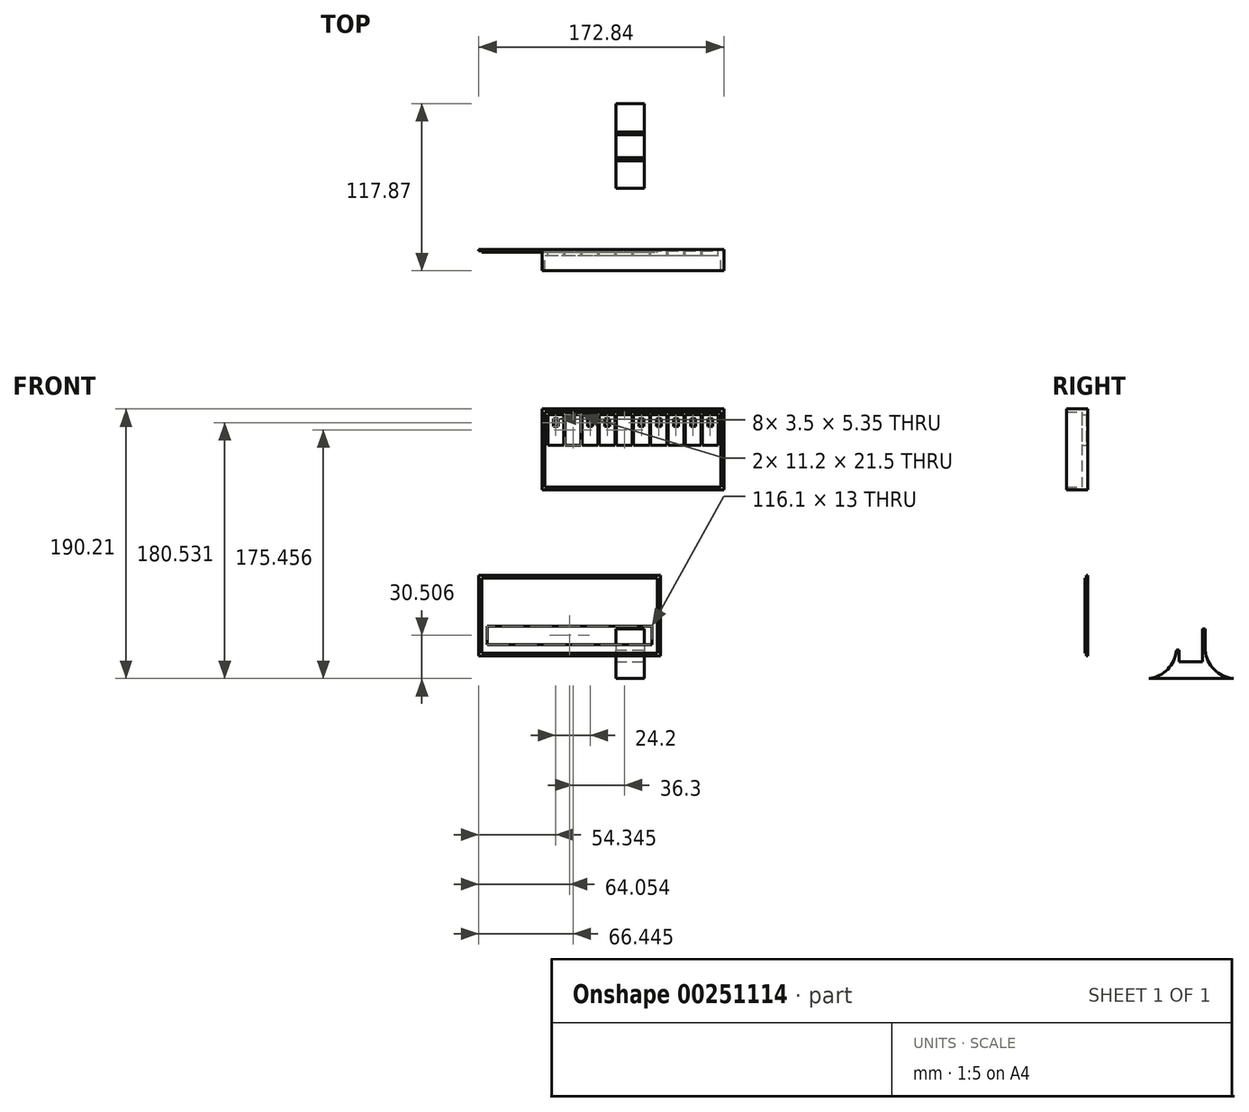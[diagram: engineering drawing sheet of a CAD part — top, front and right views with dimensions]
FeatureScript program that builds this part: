
annotation { "Feature Type Name" : "Feature", "Feature Type Description" : "" }
export const myFeature = defineFeature(function(context is Context, id is Id, definition is map)
    precondition{}
    {
        {
            var Q0;
            Q0=qCreatedBy(makeId("Front.planeOp"),FACE);
            var sketch = newSketch(context, id + "F0", { "sketchPlane" : qUnion([Q0])});
            skLineSegment(sketch, "E0.bottom", {"start": v(-72.05, 26.77) * mm, "end": v(56.05, 26.77) * mm});
            skLineSegment(sketch, "E0.top", {"start": v(-72.05, -30.23) * mm, "end": v(56.05, -30.23) * mm});
            skLineSegment(sketch, "E0.left", {"start": v(-72.05, 26.77) * mm, "end": v(-72.05, -30.23) * mm});
            skLineSegment(sketch, "E0.right", {"start": v(56.05, 26.77) * mm, "end": v(56.05, -30.23) * mm});
            skLineSegment(sketch, "E1", {"start": v(-72.05, 26.77) * mm, "end": v(-70.05, 26.77) * mm});
            skLineSegment(sketch, "E2.bottom", {"start": v(-70.05, 24.77) * mm, "end": v(54.05, 24.77) * mm});
            skLineSegment(sketch, "E2.top", {"start": v(-70.05, -28.23) * mm, "end": v(54.05, -28.23) * mm});
            skLineSegment(sketch, "E2.left", {"start": v(-70.05, 24.77) * mm, "end": v(-70.05, -28.23) * mm});
            skLineSegment(sketch, "E2.right", {"start": v(54.05, 24.77) * mm, "end": v(54.05, -28.23) * mm});
            skLineSegment(sketch, "E3", {"start": v(-70.05, 24.77) * mm, "end": v(-68.05, 24.77) * mm});
            skLineSegment(sketch, "E4", {"start": v(-68.05, 22.77) * mm, "end": v(-56.85, 22.77) * mm});
            skLineSegment(sketch, "E5", {"start": v(-55.95, 22.77) * mm, "end": v(-44.75, 22.77) * mm});
            skLineSegment(sketch, "E6", {"start": v(-43.85, 22.77) * mm, "end": v(-32.65, 22.77) * mm});
            skLineSegment(sketch, "E7", {"start": v(-31.75, 22.77) * mm, "end": v(-20.55, 22.77) * mm});
            skLineSegment(sketch, "E8", {"start": v(-19.65, 22.77) * mm, "end": v(-8.45, 22.77) * mm});
            skLineSegment(sketch, "E9", {"start": v(-7.55, 22.77) * mm, "end": v(3.65, 22.77) * mm});
            skLineSegment(sketch, "E10", {"start": v(4.55, 22.77) * mm, "end": v(15.75, 22.77) * mm});
            skLineSegment(sketch, "E11", {"start": v(16.65, 22.77) * mm, "end": v(27.85, 22.77) * mm});
            skLineSegment(sketch, "E12", {"start": v(28.75, 22.77) * mm, "end": v(39.95, 22.77) * mm});
            skLineSegment(sketch, "E13", {"start": v(40.85, 22.77) * mm, "end": v(48.79, 22.77) * mm});
            skLineSegment(sketch, "E14.top", {"start": v(-68.05, 1.27) * mm, "end": v(-56.85, 1.27) * mm});
            skLineSegment(sketch, "E14.left", {"start": v(-68.05, 22.77) * mm, "end": v(-68.05, 1.27) * mm});
            skLineSegment(sketch, "E14.right", {"start": v(-56.85, 22.77) * mm, "end": v(-56.85, 1.27) * mm});
            skLineSegment(sketch, "E15.top", {"start": v(-55.95, 1.27) * mm, "end": v(-44.75, 1.27) * mm});
            skLineSegment(sketch, "E15.left", {"start": v(-55.95, 22.77) * mm, "end": v(-55.95, 1.27) * mm});
            skLineSegment(sketch, "E15.right", {"start": v(-44.75, 22.77) * mm, "end": v(-44.75, 1.27) * mm});
            skLineSegment(sketch, "E16.top", {"start": v(-43.85, 1.27) * mm, "end": v(-32.65, 1.27) * mm});
            skLineSegment(sketch, "E16.left", {"start": v(-43.85, 22.77) * mm, "end": v(-43.85, 1.27) * mm});
            skLineSegment(sketch, "E16.right", {"start": v(-32.65, 22.77) * mm, "end": v(-32.65, 1.27) * mm});
            skLineSegment(sketch, "E17.top", {"start": v(-31.75, 1.27) * mm, "end": v(-20.55, 1.27) * mm});
            skLineSegment(sketch, "E17.left", {"start": v(-31.75, 22.77) * mm, "end": v(-31.75, 1.27) * mm});
            skLineSegment(sketch, "E17.right", {"start": v(-20.55, 22.77) * mm, "end": v(-20.55, 1.27) * mm});
            skLineSegment(sketch, "E18.top", {"start": v(-19.65, 1.27) * mm, "end": v(-8.45, 1.27) * mm});
            skLineSegment(sketch, "E18.left", {"start": v(-19.65, 22.77) * mm, "end": v(-19.65, 1.27) * mm});
            skLineSegment(sketch, "E18.right", {"start": v(-8.45, 22.77) * mm, "end": v(-8.45, 1.27) * mm});
            skLineSegment(sketch, "E19.top", {"start": v(-7.55, 1.27) * mm, "end": v(3.65, 1.27) * mm});
            skLineSegment(sketch, "E19.left", {"start": v(-7.55, 22.77) * mm, "end": v(-7.55, 1.27) * mm});
            skLineSegment(sketch, "E19.right", {"start": v(3.65, 22.77) * mm, "end": v(3.65, 1.27) * mm});
            skLineSegment(sketch, "E20.top", {"start": v(4.55, 1.27) * mm, "end": v(15.75, 1.27) * mm});
            skLineSegment(sketch, "E20.left", {"start": v(4.55, 22.77) * mm, "end": v(4.55, 1.27) * mm});
            skLineSegment(sketch, "E20.right", {"start": v(15.75, 22.77) * mm, "end": v(15.75, 1.27) * mm});
            skLineSegment(sketch, "E21.top", {"start": v(16.65, 1.27) * mm, "end": v(27.85, 1.27) * mm});
            skLineSegment(sketch, "E21.left", {"start": v(16.65, 22.77) * mm, "end": v(16.65, 1.27) * mm});
            skLineSegment(sketch, "E21.right", {"start": v(27.85, 22.77) * mm, "end": v(27.85, 1.27) * mm});
            skLineSegment(sketch, "E22.top", {"start": v(28.75, 1.27) * mm, "end": v(39.95, 1.27) * mm});
            skLineSegment(sketch, "E22.left", {"start": v(28.75, 22.77) * mm, "end": v(28.75, 1.27) * mm});
            skLineSegment(sketch, "E22.right", {"start": v(39.95, 22.77) * mm, "end": v(39.95, 1.27) * mm});
            skLineSegment(sketch, "E23.bottom", {"start": v(40.85, 22.77) * mm, "end": v(52.05, 22.77) * mm});
            skLineSegment(sketch, "E23.top", {"start": v(40.85, 1.27) * mm, "end": v(52.05, 1.27) * mm});
            skLineSegment(sketch, "E23.left", {"start": v(40.85, 22.77) * mm, "end": v(40.85, 1.27) * mm});
            skLineSegment(sketch, "E23.right", {"start": v(52.05, 22.77) * mm, "end": v(52.05, 1.27) * mm});
            skLineSegment(sketch, "E24", {"start": v(-68.05, 22.77) * mm, "end": v(-64.2, 22.77) * mm});
            skLineSegment(sketch, "E25", {"start": v(-55.95, 22.77) * mm, "end": v(-52.1, 22.77) * mm});
            skLineSegment(sketch, "E26", {"start": v(-43.85, 22.77) * mm, "end": v(-40, 22.77) * mm});
            skLineSegment(sketch, "E27", {"start": v(-31.75, 22.77) * mm, "end": v(-27.9, 22.77) * mm});
            skLineSegment(sketch, "E28", {"start": v(-19.65, 22.77) * mm, "end": v(-15.8, 22.77) * mm});
            skLineSegment(sketch, "E29", {"start": v(-7.55, 22.77) * mm, "end": v(-3.7, 22.77) * mm});
            skLineSegment(sketch, "E30", {"start": v(4.55, 22.77) * mm, "end": v(8.4, 22.77) * mm});
            skLineSegment(sketch, "E31", {"start": v(16.65, 22.77) * mm, "end": v(20.5, 22.77) * mm});
            skLineSegment(sketch, "E32", {"start": v(28.75, 22.77) * mm, "end": v(32.6, 22.77) * mm});
            skLineSegment(sketch, "E33", {"start": v(40.85, 22.77) * mm, "end": v(44.7, 22.77) * mm});
            skLineSegment(sketch, "E34.bottom", {"start": v(-64.2, 19.77) * mm, "end": v(-60.7, 19.77) * mm});
            skLineSegment(sketch, "E34.top", {"start": v(-64.2, 14.42) * mm, "end": v(-60.7, 14.42) * mm});
            skLineSegment(sketch, "E34.left", {"start": v(-64.2, 19.77) * mm, "end": v(-64.2, 14.42) * mm});
            skLineSegment(sketch, "E34.right", {"start": v(-60.7, 19.77) * mm, "end": v(-60.7, 14.42) * mm});
            skLineSegment(sketch, "E35", {"start": v(-52.1, 22.77) * mm, "end": v(-52.1, 19.77) * mm});
            skLineSegment(sketch, "E36.bottom", {"start": v(-52.1, 19.77) * mm, "end": v(-48.6, 19.77) * mm});
            skLineSegment(sketch, "E36.top", {"start": v(-52.1, 14.42) * mm, "end": v(-48.6, 14.42) * mm});
            skLineSegment(sketch, "E36.left", {"start": v(-52.1, 19.77) * mm, "end": v(-52.1, 14.42) * mm});
            skLineSegment(sketch, "E36.right", {"start": v(-48.6, 19.77) * mm, "end": v(-48.6, 14.42) * mm});
            skLineSegment(sketch, "E37", {"start": v(-40, 22.77) * mm, "end": v(-40, 19.77) * mm});
            skLineSegment(sketch, "E38.bottom", {"start": v(-40, 19.77) * mm, "end": v(-36.5, 19.77) * mm});
            skLineSegment(sketch, "E38.top", {"start": v(-40, 14.42) * mm, "end": v(-36.5, 14.42) * mm});
            skLineSegment(sketch, "E38.left", {"start": v(-40, 19.77) * mm, "end": v(-40, 14.42) * mm});
            skLineSegment(sketch, "E38.right", {"start": v(-36.5, 19.77) * mm, "end": v(-36.5, 14.42) * mm});
            skLineSegment(sketch, "E39", {"start": v(-27.9, 22.77) * mm, "end": v(-27.9, 19.77) * mm});
            skLineSegment(sketch, "E40.bottom", {"start": v(-27.9, 19.77) * mm, "end": v(-24.4, 19.77) * mm});
            skLineSegment(sketch, "E40.top", {"start": v(-27.9, 14.42) * mm, "end": v(-24.4, 14.42) * mm});
            skLineSegment(sketch, "E40.left", {"start": v(-27.9, 19.77) * mm, "end": v(-27.9, 14.42) * mm});
            skLineSegment(sketch, "E40.right", {"start": v(-24.4, 19.77) * mm, "end": v(-24.4, 14.42) * mm});
            skLineSegment(sketch, "E41", {"start": v(-15.8, 22.77) * mm, "end": v(-15.8, 19.77) * mm});
            skLineSegment(sketch, "E42.bottom", {"start": v(-15.8, 19.77) * mm, "end": v(-12.3, 19.77) * mm});
            skLineSegment(sketch, "E42.top", {"start": v(-15.8, 14.42) * mm, "end": v(-12.3, 14.42) * mm});
            skLineSegment(sketch, "E42.left", {"start": v(-15.8, 19.77) * mm, "end": v(-15.8, 14.42) * mm});
            skLineSegment(sketch, "E42.right", {"start": v(-12.3, 19.77) * mm, "end": v(-12.3, 14.42) * mm});
            skLineSegment(sketch, "E43", {"start": v(-3.7, 22.77) * mm, "end": v(-3.7, 19.77) * mm});
            skLineSegment(sketch, "E44.bottom", {"start": v(-3.7, 19.77) * mm, "end": v(-0.2, 19.77) * mm});
            skLineSegment(sketch, "E44.top", {"start": v(-3.7, 14.42) * mm, "end": v(-0.2, 14.42) * mm});
            skLineSegment(sketch, "E44.left", {"start": v(-3.7, 19.77) * mm, "end": v(-3.7, 14.42) * mm});
            skLineSegment(sketch, "E44.right", {"start": v(-0.2, 19.77) * mm, "end": v(-0.2, 14.42) * mm});
            skLineSegment(sketch, "E45", {"start": v(8.4, 22.77) * mm, "end": v(8.4, 19.77) * mm});
            skLineSegment(sketch, "E46.bottom", {"start": v(8.4, 19.77) * mm, "end": v(11.9, 19.77) * mm});
            skLineSegment(sketch, "E46.top", {"start": v(8.4, 14.42) * mm, "end": v(11.9, 14.42) * mm});
            skLineSegment(sketch, "E46.left", {"start": v(8.4, 19.77) * mm, "end": v(8.4, 14.42) * mm});
            skLineSegment(sketch, "E46.right", {"start": v(11.9, 19.77) * mm, "end": v(11.9, 14.42) * mm});
            skLineSegment(sketch, "E47", {"start": v(20.5, 22.77) * mm, "end": v(20.5, 19.77) * mm});
            skLineSegment(sketch, "E48.bottom", {"start": v(20.5, 19.77) * mm, "end": v(24, 19.77) * mm});
            skLineSegment(sketch, "E48.top", {"start": v(20.5, 14.42) * mm, "end": v(24, 14.42) * mm});
            skLineSegment(sketch, "E48.left", {"start": v(20.5, 19.77) * mm, "end": v(20.5, 14.42) * mm});
            skLineSegment(sketch, "E48.right", {"start": v(24, 19.77) * mm, "end": v(24, 14.42) * mm});
            skLineSegment(sketch, "E49", {"start": v(32.6, 22.77) * mm, "end": v(32.6, 19.77) * mm});
            skLineSegment(sketch, "E50.bottom", {"start": v(32.6, 19.77) * mm, "end": v(36.1, 19.77) * mm});
            skLineSegment(sketch, "E50.top", {"start": v(32.6, 14.42) * mm, "end": v(36.1, 14.42) * mm});
            skLineSegment(sketch, "E50.left", {"start": v(32.6, 19.77) * mm, "end": v(32.6, 14.42) * mm});
            skLineSegment(sketch, "E50.right", {"start": v(36.1, 19.77) * mm, "end": v(36.1, 14.42) * mm});
            skLineSegment(sketch, "E51", {"start": v(44.7, 22.77) * mm, "end": v(44.7, 19.77) * mm});
            skLineSegment(sketch, "E52.bottom", {"start": v(44.7, 19.77) * mm, "end": v(48.2, 19.77) * mm});
            skLineSegment(sketch, "E52.top", {"start": v(44.7, 14.42) * mm, "end": v(48.2, 14.42) * mm});
            skLineSegment(sketch, "E52.left", {"start": v(44.7, 19.77) * mm, "end": v(44.7, 14.42) * mm});
            skLineSegment(sketch, "E52.right", {"start": v(48.2, 19.77) * mm, "end": v(48.2, 14.42) * mm});
            skSolve(sketch);
        }
        {
            var Q0;
            Q0=makeQuery(id+"F0.imprint","IMPRINT",FACE,{"disambiguationData":[TD([[makeQuery(id+"F0.imprint","IMPRINT",EDGE,{"derivedFrom":sQuery(id+"F0.wireOp",EDGE,"E0.bottom")}),-1.0]])]});
            extrude(context, id + "F1", {"entities" : qUnion([Q0]), "depth" : 15 * mm});
        }
        {
            var Q0;
            Q0=makeQuery(id+"F0.imprint","IMPRINT",FACE,{"disambiguationData":[TD([[makeQuery(id+"F0.imprint","IMPRINT",EDGE,{"derivedFrom":sQuery(id+"F0.wireOp",EDGE,"E2.bottom")}),-1.0]])]});
            extrude(context, id + "F2", {"entities" : qUnion([Q0]), "operationType" : NewBodyOperationType.ADD, "depth" : 4.2 * mm});
        }
        {
            var Q0;
            Q0=makeQuery(id+"F0.imprint","IMPRINT",FACE,{"disambiguationData":[TD([[makeQuery(id+"F0.imprint","IMPRINT",EDGE,{"derivedFrom":sQuery(id+"F0.wireOp",EDGE,"E4")}),-1.0]])]});
            var Q1;
            Q1=makeQuery(id+"F0.imprint","IMPRINT",FACE,{"disambiguationData":[TD([[makeQuery(id+"F0.imprint","IMPRINT",EDGE,{"derivedFrom":sQuery(id+"F0.wireOp",EDGE,"E5")}),-1.0]])]});
            var Q2;
            Q2=makeQuery(id+"F0.imprint","IMPRINT",FACE,{"disambiguationData":[TD([[makeQuery(id+"F0.imprint","IMPRINT",EDGE,{"derivedFrom":sQuery(id+"F0.wireOp",EDGE,"E6")}),-1.0]])]});
            var Q3;
            Q3=makeQuery(id+"F0.imprint","IMPRINT",FACE,{"disambiguationData":[TD([[makeQuery(id+"F0.imprint","IMPRINT",EDGE,{"derivedFrom":sQuery(id+"F0.wireOp",EDGE,"E7")}),-1.0]])]});
            var Q4;
            Q4=makeQuery(id+"F0.imprint","IMPRINT",FACE,{"disambiguationData":[TD([[makeQuery(id+"F0.imprint","IMPRINT",EDGE,{"derivedFrom":sQuery(id+"F0.wireOp",EDGE,"E8")}),-1.0]])]});
            var Q5;
            Q5=makeQuery(id+"F0.imprint","IMPRINT",FACE,{"disambiguationData":[TD([[makeQuery(id+"F0.imprint","IMPRINT",EDGE,{"derivedFrom":sQuery(id+"F0.wireOp",EDGE,"E9")}),-1.0]])]});
            var Q6;
            Q6=makeQuery(id+"F0.imprint","IMPRINT",FACE,{"disambiguationData":[TD([[makeQuery(id+"F0.imprint","IMPRINT",EDGE,{"derivedFrom":sQuery(id+"F0.wireOp",EDGE,"E10")}),-1.0]])]});
            var Q7;
            Q7=makeQuery(id+"F0.imprint","IMPRINT",FACE,{"disambiguationData":[TD([[makeQuery(id+"F0.imprint","IMPRINT",EDGE,{"derivedFrom":sQuery(id+"F0.wireOp",EDGE,"E11")}),-1.0]])]});
            var Q8;
            Q8=makeQuery(id+"F0.imprint","IMPRINT",FACE,{"disambiguationData":[TD([[makeQuery(id+"F0.imprint","IMPRINT",EDGE,{"derivedFrom":sQuery(id+"F0.wireOp",EDGE,"E12")}),-1.0]])]});
            var Q9;
            Q9=makeQuery(id+"F0.imprint","IMPRINT",FACE,{"disambiguationData":[TD([[makeQuery(id+"F0.imprint","IMPRINT",EDGE,{"derivedFrom":sQuery(id+"F0.wireOp",EDGE,"E23.top")}),1.0]])]});
            extrude(context, id + "F3", {"entities" : qUnion([Q0, Q1, Q2, Q3, Q4, Q5, Q6, Q7, Q8, Q9]), "operationType" : NewBodyOperationType.ADD, "depth" : 1 * mm});
        }
        {
            var Q0;
            Q0=qCreatedBy(makeId("Front.planeOp"),FACE);
            var sketch = newSketch(context, id + "F4", { "sketchPlane" : qUnion([Q0])});
            skLineSegment(sketch, "E53.bottom", {"start": v(-116.79, -90.43) * mm, "end": v(11.31, -90.43) * mm});
            skLineSegment(sketch, "E53.top", {"start": v(-116.79, -147.43) * mm, "end": v(11.31, -147.43) * mm});
            skLineSegment(sketch, "E53.left", {"start": v(-116.79, -90.43) * mm, "end": v(-116.79, -147.43) * mm});
            skLineSegment(sketch, "E53.right", {"start": v(11.31, -90.43) * mm, "end": v(11.31, -147.43) * mm});
            skLineSegment(sketch, "E54", {"start": v(-116.79, -90.43) * mm, "end": v(-114.79, -90.43) * mm});
            skLineSegment(sketch, "E55.bottom", {"start": v(-114.79, -92.43) * mm, "end": v(9.31, -92.43) * mm});
            skLineSegment(sketch, "E55.top", {"start": v(-114.79, -145.43) * mm, "end": v(9.31, -145.43) * mm});
            skLineSegment(sketch, "E55.left", {"start": v(-114.79, -92.43) * mm, "end": v(-114.79, -145.43) * mm});
            skLineSegment(sketch, "E55.right", {"start": v(9.31, -92.43) * mm, "end": v(9.31, -145.43) * mm});
            skLineSegment(sketch, "E56", {"start": v(-114.79, -92.43) * mm, "end": v(-112.79, -92.43) * mm});
            skLineSegment(sketch, "E57", {"start": v(-114.79, -145.43) * mm, "end": v(-114.79, -139.43) * mm});
            skLineSegment(sketch, "E58", {"start": v(-110.79, -139.43) * mm, "end": v(-110.79, -126.43) * mm});
            skLineSegment(sketch, "E59", {"start": v(-110.79, -126.43) * mm, "end": v(5.31, -126.43) * mm});
            skLineSegment(sketch, "E60", {"start": v(-110.79, -139.43) * mm, "end": v(5.31, -139.43) * mm});
            skLineSegment(sketch, "E61", {"start": v(5.31, -139.43) * mm, "end": v(5.31, -126.43) * mm});
            skSolve(sketch);
        }
        {
            var Q0;
            Q0=makeQuery(id+"F4.imprint","IMPRINT",FACE,{"disambiguationData":[TD([[makeQuery(id+"F4.imprint","IMPRINT",EDGE,{"derivedFrom":sQuery(id+"F4.wireOp",EDGE,"E55.bottom")}),-1.0]])]});
            extrude(context, id + "F5", {"entities" : qUnion([Q0]), "depth" : 2 * mm});
        }
        {
            var Q0;
            Q0=makeQuery(id+"F4.imprint","IMPRINT",FACE,{"disambiguationData":[TD([[makeQuery(id+"F4.imprint","IMPRINT",EDGE,{"derivedFrom":sQuery(id+"F4.wireOp",EDGE,"E53.bottom")}),-1.0]])]});
            extrude(context, id + "F6", {"entities" : qUnion([Q0]), "operationType" : NewBodyOperationType.ADD, "depth" : 1 * mm});
        }
        {
            var Q0;
            Q0=qCreatedBy(makeId("Right.planeOp"),FACE);
            var sketch = newSketch(context, id + "F7", { "sketchPlane" : qUnion([Q0])});
            skLineSegment(sketch, "E62.bottom", {"start": v(62.67, -143.44) * mm, "end": v(64.67, -143.44) * mm});
            skLineSegment(sketch, "E63", {"start": v(64.67, -151.44) * mm, "end": v(80.87, -151.44) * mm});
            skLineSegment(sketch, "E64", {"start": v(64.67, -143.44) * mm, "end": v(64.67, -151.44) * mm});
            skLineSegment(sketch, "E65", {"start": v(80.87, -151.44) * mm, "end": v(80.87, -143.44) * mm});
            skLineSegment(sketch, "E66", {"start": v(80.87, -143.44) * mm, "end": v(82.87, -143.44) * mm});
            skLineSegment(sketch, "E67", {"start": v(63.17, -163.44) * mm, "end": v(43.17, -163.44) * mm});
            skArc(sketch, "E68", {"start": v(43.17, -163.44) * mm, "mid": v(56.42, -156.86) * mm, "end": v(62.67, -143.44) * mm});
            skLineSegment(sketch, "E69", {"start": v(63.17, -163.44) * mm, "end": v(82.87, -163.44) * mm});
            skLineSegment(sketch, "E70", {"start": v(82.87, -163.44) * mm, "end": v(102.87, -163.44) * mm});
            skArc(sketch, "E71", {"start": v(82.87, -143.44) * mm, "mid": v(89.3, -157) * mm, "end": v(102.87, -163.44) * mm});
            skSolve(sketch);
        }
        {
            var Q0;
            Q0=makeQuery(id+"F7.imprint","IMPRINT",FACE,{"disambiguationData":[TD([[makeQuery(id+"F7.imprint","IMPRINT",EDGE,{"derivedFrom":sQuery(id+"F7.wireOp",EDGE,"E62.bottom")}),-1.0]])]});
            extrude(context, id + "F8", {"entities" : qUnion([Q0]), "oppositeDirection" : true, "depth" : 20 * mm});
        }
        {
            var Q0;
            Q0=makeQuery(id+"F8.opExtrude","SWEPT_FACE",FACE,{"disambiguationData":[OSD([sQuery(id+"F7.wireOp",EDGE,"E66")])]});
            extrude(context, id + "F9", {"entities" : qUnion([Q0]), "operationType" : NewBodyOperationType.ADD, "depth" : 15 * mm});
        }
    });
